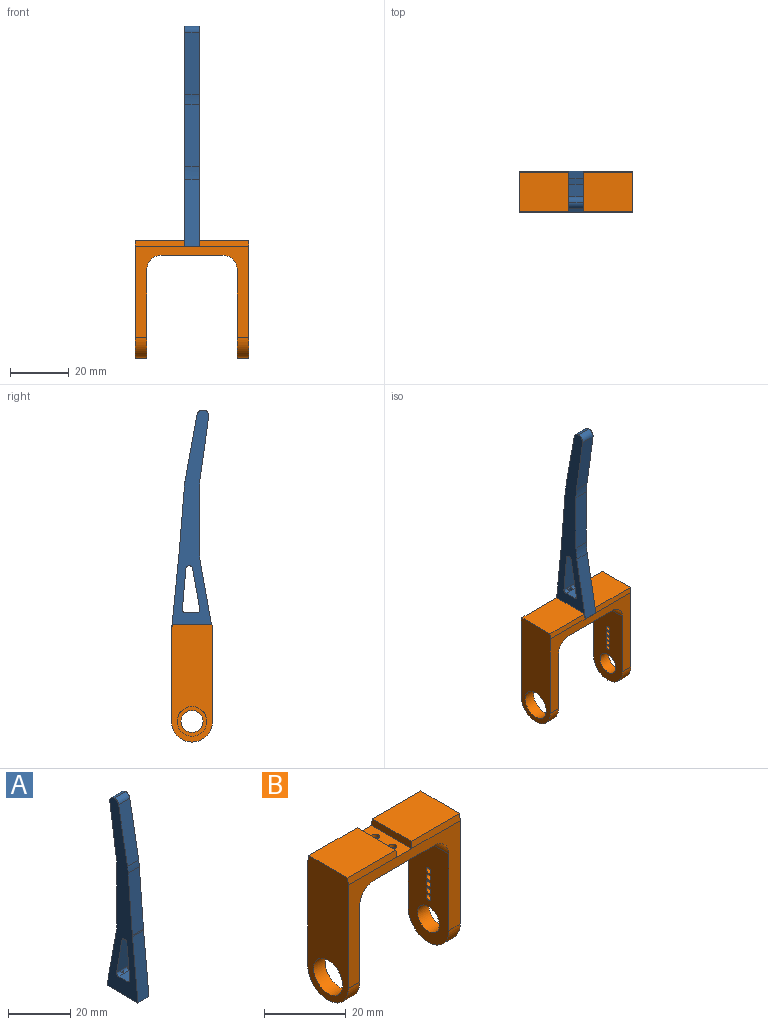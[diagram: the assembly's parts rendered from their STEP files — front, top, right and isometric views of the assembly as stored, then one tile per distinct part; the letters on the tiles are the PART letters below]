
ASSEMBLY  parts=2 mates=1
PART A: 30 faces, bbox 5.1x14x75 mm
  f0: plane 5x0mm, normal (0,-1,0), area 0mm2, adj f2,f4,f7
  f1: plane 5.08x0.03mm, normal (0,0,1), area 0.1mm2, adj f2,f3,f16,f17
  f2: plane 75x14mm, normal (-1,0,0), area 458mm2, adj f0,f1,f4,f5,f6,f7,f8,f9
  f3: plane 75x14mm, normal (1,0,0), area 458mm2, adj f1,f4,f6,f7,f8,f9,f10,f11
  f4: plane 14x5mm, normal (0,0,-1), area 66mm2, adj f0,f2,f3,f5,f26,f28
  f5: plane 5x0mm, normal (0,1,0), area 0mm2, adj f2,f4,f14
  f6: plane 22.14x5.08mm, normal (0,-0.98,0.18), area 113.9mm2, adj f2,f3,f17,f20
  f7: plane 24.76x5.03mm, normal (0,-1,0.1), area 124.7mm2, adj f0,f2,f3,f21
  f8: plane 23.53x5.05mm, normal (0,-1,0.08), area 118.9mm2, adj f2,f3,f20,f21
  f9: plane 14x5.02mm, normal (0,1,-0.09), area 70.5mm2, adj f2,f3,f22,f25
  f10: plane 5.01x3.97mm, normal (0,0,1), area 19.8mm2, adj f2,f3,f24,f25,f26
  f11: plane 14x5.02mm, normal (0,-0.98,-0.17), area 71.3mm2, adj f2,f3,f23,f24
  f12: plane 5.02x0.28mm, normal (0,0,-1), area 1.4mm2, adj f2,f3,f22,f23
  f13: plane 21x5.07mm, normal (0,0.99,-0.14), area 107.3mm2, adj f2,f3,f16,f18
  f14: plane 22.81x5.02mm, normal (0,0.98,0.18), area 116.1mm2, adj f2,f3,f5,f19
  f15: plane 21.03x5.05mm, normal (0,1,0), area 105.9mm2, adj f2,f3,f18,f19
  f16: cylinder r=2mm len=5.08mm, axis (-1,0,0), area 17.4mm2, adj f1,f2,f3,f13
  f17: cylinder r=2mm len=5.08mm, axis (-1,0,0), area 14.1mm2, adj f1,f2,f3,f6
  f18: cylinder r=25mm len=5.05mm, axis (-1,0,0), area 17.6mm2, adj f2,f3,f13,f15
  f19: cylinder r=25mm len=5.03mm, axis (1,0,0), area 22.4mm2, adj f2,f3,f14,f15
  f20: cylinder r=25mm len=5.05mm, axis (1,0,0), area 12.4mm2, adj f2,f3,f6,f8
  f21: cylinder r=25mm len=5.03mm, axis (1,0,0), area 2.5mm2, adj f2,f3,f7,f8
  f22: cylinder r=1mm len=5.02mm, axis (-1,0,0), area 7.5mm2, adj f2,f3,f9,f12
  f23: cylinder r=1mm len=5.02mm, axis (-1,0,0), area 7mm2, adj f2,f3,f11,f12
  f24: cylinder r=1mm len=5.01mm, axis (-1,0,0), area 8.3mm2, adj f2,f3,f10,f11,f28,f29
  f25: cylinder r=1mm len=5.01mm, axis (-1,0,0), area 6.8mm2, adj f2,f3,f9,f10,f26,f27
  f26: cylinder r=0.8mm len=6.5mm, axis (0,0,-1), area 31.5mm2, adj f4,f10,f25,f27
  f27: plane 1.57x0.64mm, normal (0,0,-1), area 0.8mm2, adj f25,f26
  f28: cylinder r=0.8mm len=6.5mm, axis (0,0,-1), area 32.3mm2, adj f4,f24,f29
  f29: plane 1.6x1.26mm, normal (0,0,-1), area 1.7mm2, adj f24,f28
PART B: 37 faces, bbox 38.7x14x40 mm
  f0: cylinder r=0.8mm len=2mm, axis (1,0,0), area 10.1mm2, adj f7,f34
  f1: cylinder r=0.8mm len=2mm, axis (1,0,0), area 10.1mm2, adj f7,f34
  f2: cylinder r=0.8mm len=2mm, axis (1,0,0), area 10.1mm2, adj f7,f34
  f3: cylinder r=0.8mm len=2mm, axis (1,0,0), area 10.1mm2, adj f7,f34
  f4: cylinder r=0.8mm len=2mm, axis (1,0,0), area 10.1mm2, adj f7,f34
  f5: plane 14x2.1mm, normal (-1,0,0), area 28.9mm2, adj f6,f8,f10,f16,f26,f28
  f6: plane 38.7x31mm, normal (0,-1,0), area 350.3mm2, adj f5,f7,f9,f11,f12,f13,f14,f16
  f7: plane 30x14mm, normal (-1,0,0), area 344.7mm2, adj f0,f1,f2,f3,f4,f6,f8,f17
  f8: plane 38.7x31mm, normal (0,1,0), area 350.3mm2, adj f5,f7,f9,f11,f12,f13,f14,f16
  f9: plane 40x14mm, normal (1,0,0), area 435.4mm2, adj f6,f8,f10,f17,f26,f28,f30,f31
  f10: plane 16.7x13.45mm, normal (0,0,1), area 224.6mm2, adj f5,f9,f26,f28
  f11: plane 20.7x14mm, normal (0,0,-1), area 268.3mm2, adj f6,f8,f21,f23,f35,f36
  f12: plane 14x2.1mm, normal (1,0,0), area 28.9mm2, adj f6,f8,f15,f16,f25,f27
  f13: plane 30x14mm, normal (1,0,0), area 318.9mm2, adj f6,f8,f18,f29,f36
  f14: plane 40x14mm, normal (-1,0,0), area 458.3mm2, adj f6,f8,f15,f18,f25,f27,f29
  f15: plane 16.7x13.45mm, normal (0,0,1), area 224.6mm2, adj f12,f14,f25,f27
  f16: plane 14x5.3mm, normal (0,0,1), area 67.9mm2, adj f5,f6,f8,f12,f19,f20
  f17: cylinder r=7mm len=14mm, axis (1,0,0), area 88mm2, adj f6,f7,f8,f9
  f18: cylinder r=7mm len=14mm, axis (-1,0,0), area 88mm2, adj f6,f8,f13,f14
  f19: cylinder r=1mm len=2mm, axis (0,0,1), area 6.3mm2, adj f16,f24
  f20: cylinder r=1mm len=2mm, axis (0,0,1), area 6.3mm2, adj f16,f22
  f21: cylinder r=1.85mm len=3.7mm, axis (0,0,1), area 22.1mm2, adj f11,f22
  f22: plane 3.7x3.7mm, normal (0,0,-1), area 7.6mm2, adj f20,f21
  f23: cylinder r=1.85mm len=3.7mm, axis (0,0,1), area 22.1mm2, adj f11,f24
  f24: plane 3.7x3.7mm, normal (0,0,-1), area 7.6mm2, adj f19,f23
  f25: plane 16.7x2mm, normal (0,0.99,0.17), area 33.9mm2, adj f8,f12,f14,f15
  f26: plane 16.7x2mm, normal (0,0.99,0.17), area 33.9mm2, adj f5,f8,f9,f10
  f27: plane 16.7x2mm, normal (0,-1,0.1), area 33.6mm2, adj f6,f12,f14,f15
  f28: plane 16.7x2mm, normal (0,-1,0.1), area 33.6mm2, adj f5,f6,f9,f10
  f29: cylinder r=5.05mm len=10.1mm, axis (1,0,0), area 126.9mm2, adj f13,f14
  f30: cylinder r=3.75mm len=7.5mm, axis (1,0,0), area 80.7mm2, adj f7,f9,f31,f33,f34
  f31: plane 11.82x2mm, normal (0,-1,-0.08), area 23.7mm2, adj f9,f30,f32,f34
  f32: cylinder r=2mm len=4mm, axis (1,0,0), area 12.6mm2, adj f9,f31,f33,f34
  f33: plane 11.82x2mm, normal (0,1,-0.08), area 23.7mm2, adj f9,f30,f32,f34
  f34: plane 13.82x5.88mm, normal (1,0,0), area 48.8mm2, adj f0,f1,f2,f3,f4,f30,f31,f32
  f35: cylinder r=5mm len=14mm, axis (0,1,0), area 110mm2, adj f6,f7,f8,f11
  f36: cylinder r=5mm len=14mm, axis (0,-1,0), area 110mm2, adj f6,f8,f11,f13
PLACE A rot(axis=(0,0,1),180deg) t=(-93.48,-3.71,2.15)mm
PLACE B t=(-2.23,10.29,2.25)mm
MATE fastened A.f28 <-> B.f19  axis (0,0,-1) through (-47.86,0.29,27.78)mm
